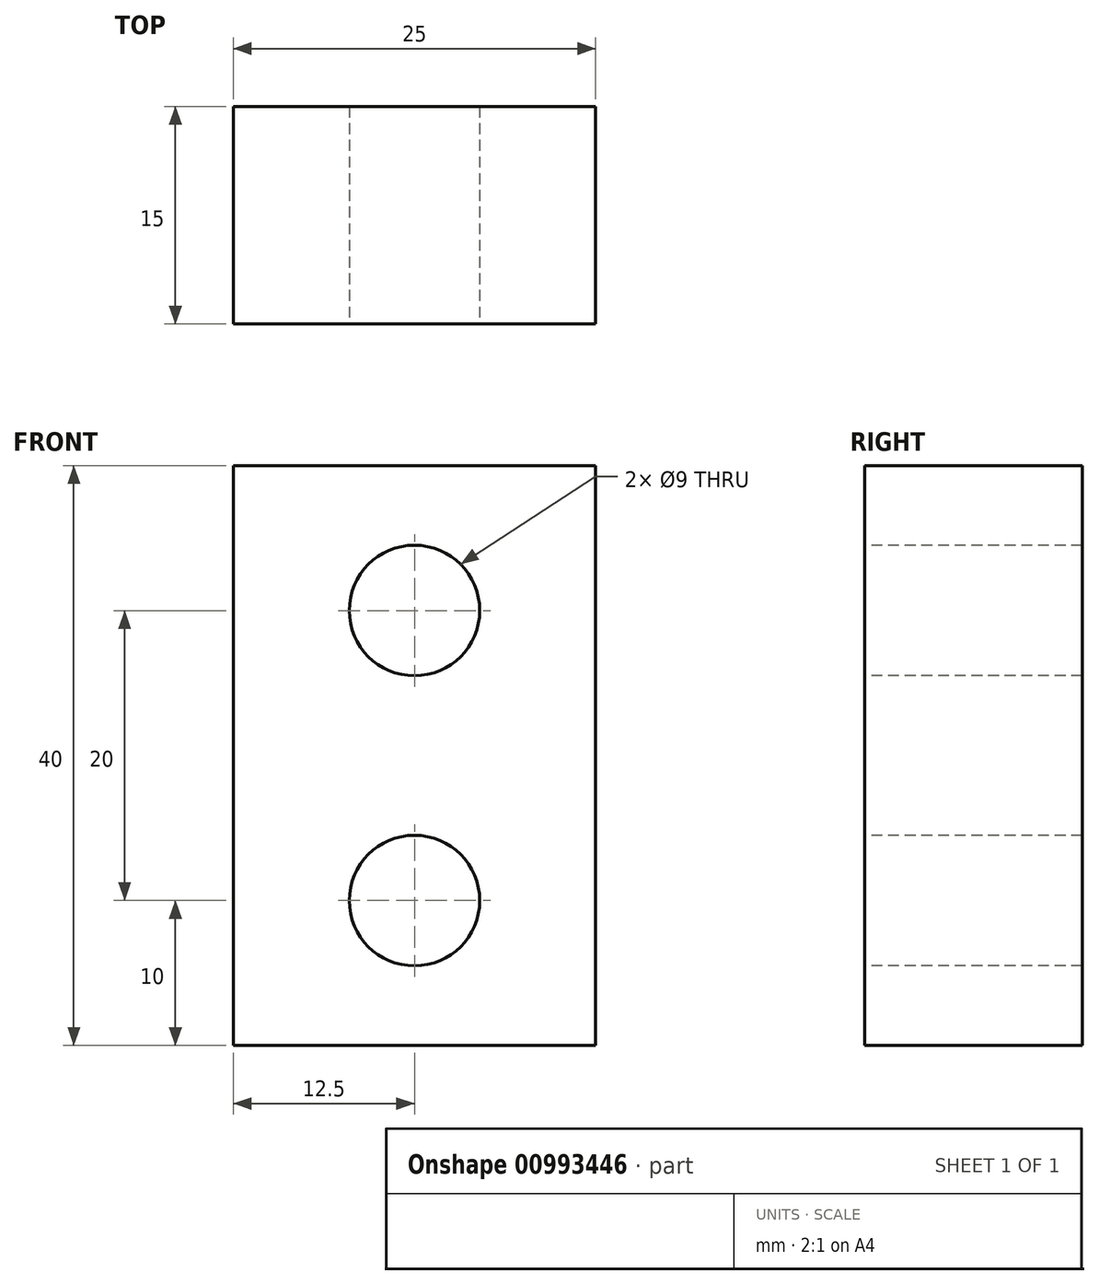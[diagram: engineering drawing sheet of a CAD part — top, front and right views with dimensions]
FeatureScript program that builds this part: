
annotation { "Feature Type Name" : "Feature", "Feature Type Description" : "" }
export const myFeature = defineFeature(function(context is Context, id is Id, definition is map)
    precondition{}
    {
        {
            var Q0;
            Q0=qCreatedBy(makeId("Front.planeOp"),FACE);
            var sketch = newSketch(context, id + "F0", { "sketchPlane" : qUnion([Q0])});
            skLineSegment(sketch, "E0.bottom", {"start": v(12.5, 20) * mm, "end": v(-12.5, 20) * mm});
            skLineSegment(sketch, "E0.top", {"start": v(12.5, -20) * mm, "end": v(-12.5, -20) * mm});
            skLineSegment(sketch, "E0.left", {"start": v(12.5, 20) * mm, "end": v(12.5, -20) * mm});
            skLineSegment(sketch, "E0.right", {"start": v(-12.5, 20) * mm, "end": v(-12.5, -20) * mm});
            skPoint(sketch, "E0.middle", {"position": v(0, 0) * mm});
            skSolve(sketch);
        }
        {
            var Q0;
            Q0 = qSketchRegion(id + "F0", true);
            extrude(context, id + "F1", {"entities" : qUnion([Q0]), "depth" : 15 * mm, "offsetDistance" : 25 * mm});
        }
        {
            var Q0;
            Q0=makeQuery(id+"F1.opExtrude","CAP_FACE",FACE,{"disambiguationData":[OSD([sQuery(id+"F0.wireOp",EDGE,"E0.bottom"),sQuery(id+"F0.wireOp",EDGE,"E0.top"),sQuery(id+"F0.wireOp",EDGE,"E0.left"),sQuery(id+"F0.wireOp",EDGE,"E0.right")])],"isStart":false});
            var sketch = newSketch(context, id + "F2", { "sketchPlane" : qUnion([Q0])});
            skPoint(sketch, "E1", {"position": v(0, 10) * mm});
            skPoint(sketch, "E2", {"position": v(0, -10) * mm});
            skSolve(sketch);
        }
        {
            var Q0;
            Q0=sQuery(id+"F2.wireOp",VERTEX,"E1");
            var Q1;
            Q1=sQuery(id+"F2.wireOp",VERTEX,"E2");
            var Q2;
            Q2=makeQuery(id+"F1.opExtrude","SWEPT_BODY",BODY,{"disambiguationData":[OSD([sQuery(id+"F0.wireOp",EDGE,"E0.bottom"),sQuery(id+"F0.wireOp",EDGE,"E0.top"),sQuery(id+"F0.wireOp",EDGE,"E0.left"),sQuery(id+"F0.wireOp",EDGE,"E0.right")])]});
            hole(context, id + "F3", {"style" : HoleStyle.SIMPLE, "endStyle" : HoleEndStyle.THROUGH, "standardTappedOrClearance" : lookupTablePath({ "fit" : "Normal", "standard" : "ISO", "size" : "M8", "type" : "Clearance" }), "standardBlindInLast" : lookupTablePath({ "fit" : "Normal", "standard" : "ISO", "engagement" : "75%", "pitch" : "1.25 mm", "size" : "M8", "type" : "Clearance & tapped" }), "holeDiameter" : 9 * mm, "majorDiameter" : 5 * mm, "isTappedThrough" : true, "tappedDepth" : 12 * mm, "tapClearance" : 3, "locations" : qUnion([Q0, Q1]), "scope" : qUnion([Q2])});
        }
    });
